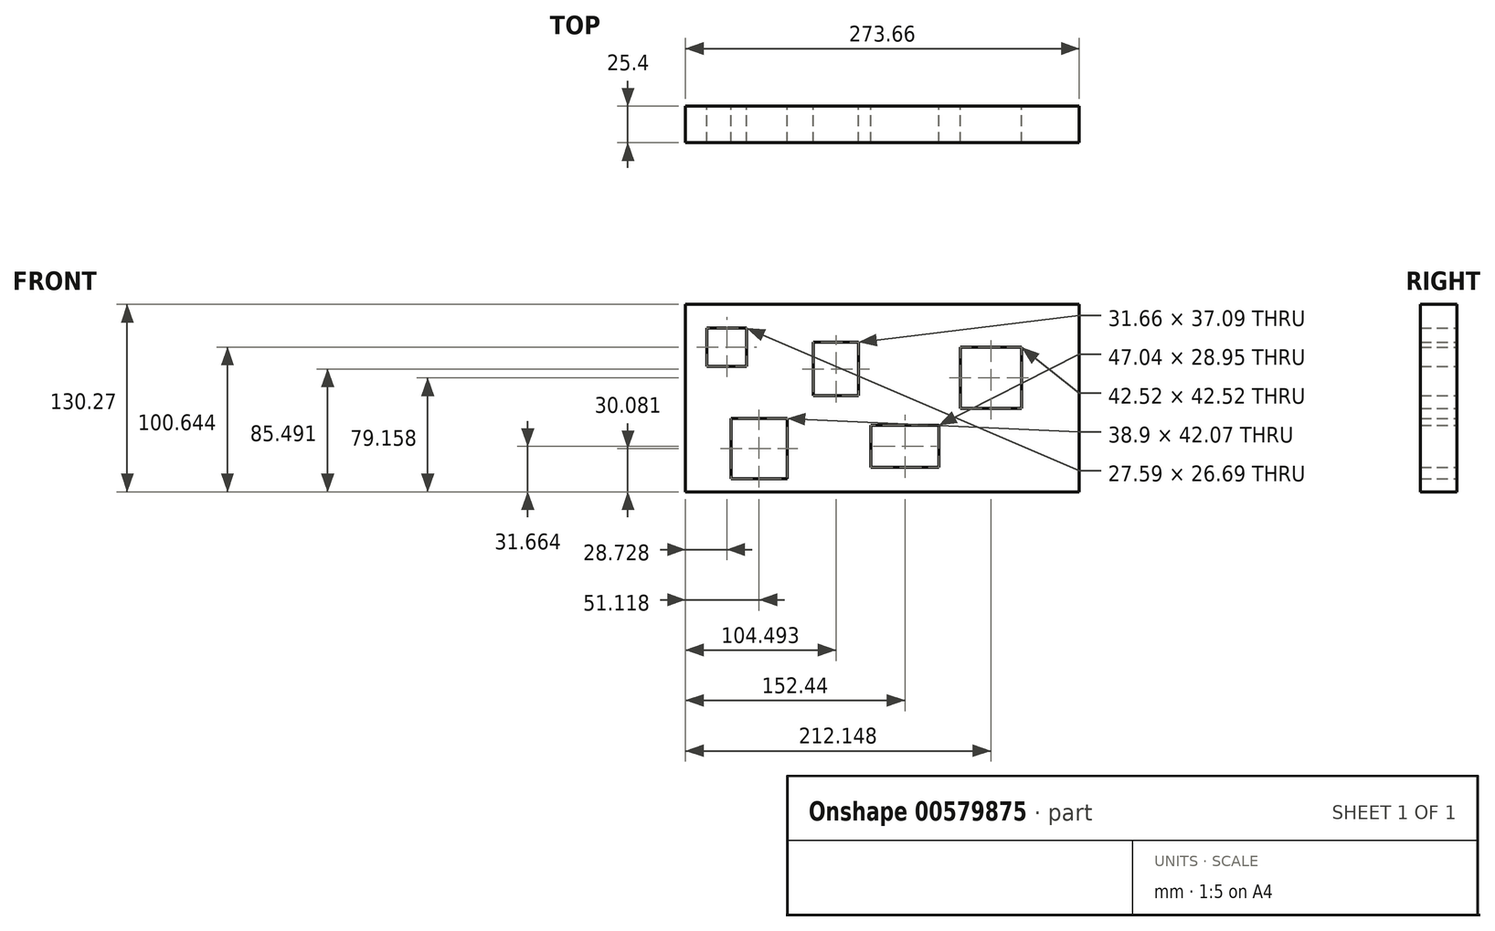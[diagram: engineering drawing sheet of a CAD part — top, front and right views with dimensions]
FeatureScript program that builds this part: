
annotation { "Feature Type Name" : "Feature", "Feature Type Description" : "" }
export const myFeature = defineFeature(function(context is Context, id is Id, definition is map)
    precondition{}
    {
        {
            var Q0;
            Q0=qCreatedBy(makeId("Front.planeOp"),FACE);
            var sketch = newSketch(context, id + "F0", { "sketchPlane" : qUnion([Q0])});
            skLineSegment(sketch, "E0.bottom", {"start": v(-138.87, 48.85) * mm, "end": v(134.8, 48.85) * mm});
            skLineSegment(sketch, "E0.top", {"start": v(-138.87, -81.42) * mm, "end": v(134.8, -81.42) * mm});
            skLineSegment(sketch, "E0.left", {"start": v(-138.87, 48.85) * mm, "end": v(-138.87, -81.42) * mm});
            skLineSegment(sketch, "E0.right", {"start": v(134.8, 48.85) * mm, "end": v(134.8, -81.42) * mm});
            skLineSegment(sketch, "E1.bottom", {"start": v(-123.94, 32.57) * mm, "end": v(-96.35, 32.57) * mm});
            skLineSegment(sketch, "E1.top", {"start": v(-123.94, 5.88) * mm, "end": v(-96.35, 5.88) * mm});
            skLineSegment(sketch, "E1.left", {"start": v(-123.94, 32.57) * mm, "end": v(-123.94, 5.88) * mm});
            skLineSegment(sketch, "E1.right", {"start": v(-96.35, 32.57) * mm, "end": v(-96.35, 5.88) * mm});
            skLineSegment(sketch, "E2.bottom", {"start": v(-107.2, -30.3) * mm, "end": v(-68.3, -30.3) * mm});
            skLineSegment(sketch, "E2.top", {"start": v(-107.2, -72.37) * mm, "end": v(-68.3, -72.37) * mm});
            skLineSegment(sketch, "E2.left", {"start": v(-107.2, -30.3) * mm, "end": v(-107.2, -72.37) * mm});
            skLineSegment(sketch, "E2.right", {"start": v(-68.3, -30.3) * mm, "end": v(-68.3, -72.37) * mm});
            skLineSegment(sketch, "E3.bottom", {"start": v(52.02, 19) * mm, "end": v(94.54, 19) * mm});
            skLineSegment(sketch, "E3.top", {"start": v(52.02, -23.52) * mm, "end": v(94.54, -23.52) * mm});
            skLineSegment(sketch, "E3.left", {"start": v(52.02, 19) * mm, "end": v(52.02, -23.52) * mm});
            skLineSegment(sketch, "E3.right", {"start": v(94.54, 19) * mm, "end": v(94.54, -23.52) * mm});
            skLineSegment(sketch, "E4.bottom", {"start": v(-18.55, 22.62) * mm, "end": v(-50.2, 22.62) * mm});
            skLineSegment(sketch, "E4.top", {"start": v(-18.55, -14.47) * mm, "end": v(-50.2, -14.47) * mm});
            skLineSegment(sketch, "E4.left", {"start": v(-18.55, 22.62) * mm, "end": v(-18.55, -14.47) * mm});
            skLineSegment(sketch, "E4.right", {"start": v(-50.2, 22.62) * mm, "end": v(-50.2, -14.47) * mm});
            skLineSegment(sketch, "E5.bottom", {"start": v(-9.95, -35.28) * mm, "end": v(37.1, -35.28) * mm});
            skLineSegment(sketch, "E5.top", {"start": v(-9.95, -64.23) * mm, "end": v(37.1, -64.23) * mm});
            skLineSegment(sketch, "E5.left", {"start": v(-9.95, -35.28) * mm, "end": v(-9.95, -64.23) * mm});
            skLineSegment(sketch, "E5.right", {"start": v(37.1, -35.28) * mm, "end": v(37.1, -64.23) * mm});
            skSolve(sketch);
        }
        {
            var Q0;
            Q0=makeQuery(id+"F0.imprint","IMPRINT",FACE,{"disambiguationData":[TD([[makeQuery(id+"F0.imprint","IMPRINT",EDGE,{"derivedFrom":sQuery(id+"F0.wireOp",EDGE,"E0.bottom")}),-1.0]])]});
            extrude(context, id + "F1", {"entities" : qUnion([Q0]), "depth" : 25.4 * mm, "offsetDistance" : 25.4 * mm});
        }
    });
